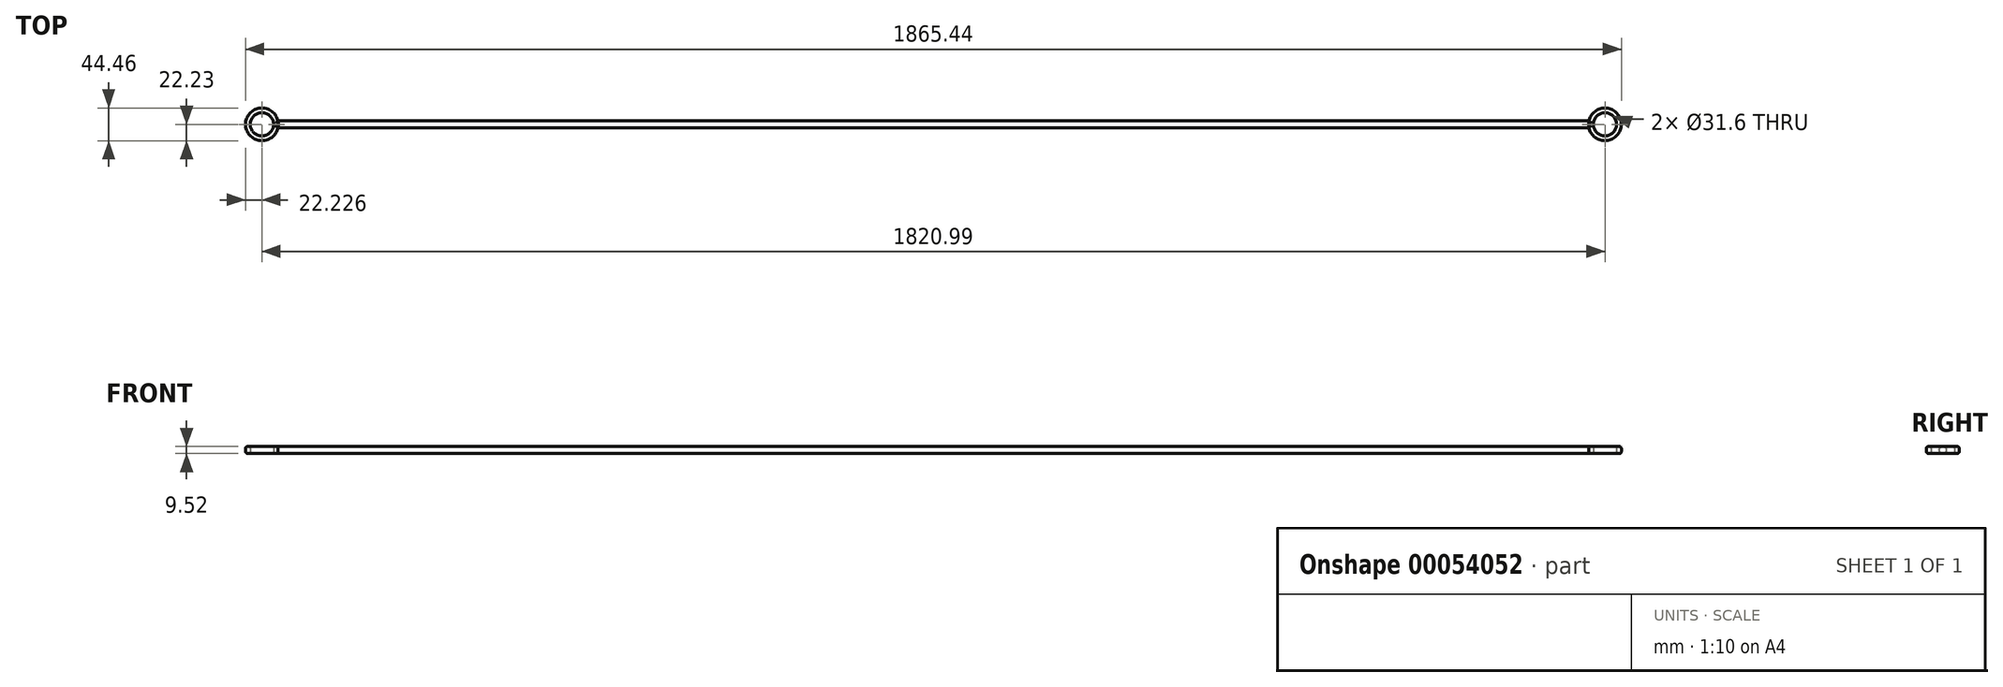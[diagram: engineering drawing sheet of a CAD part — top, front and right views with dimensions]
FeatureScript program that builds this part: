
annotation { "Feature Type Name" : "Feature", "Feature Type Description" : "" }
export const myFeature = defineFeature(function(context is Context, id is Id, definition is map)
    precondition{}
    {
        {
            var Q0;
            Q0=qCreatedBy(makeId("Right.planeOp"),FACE);
            var sketch = newSketch(context, id + "F0", { "sketchPlane" : qUnion([Q0])});
            skCircle(sketch, "E0", {"center": v(0, 0) * mm, "radius": 4.76 * mm});
            skSolve(sketch);
        }
        {
            var Q0;
            Q0=makeQuery(id+"F0.imprint","IMPRINT",FACE,{"disambiguationData":[TD([[makeQuery(id+"F0.imprint","IMPRINT",EDGE,{"derivedFrom":sQuery(id+"F0.wireOp",EDGE,"E0")}),1.0]])]});
            extrude(context, id + "F1", {"entities" : qUnion([Q0]), "depth" : 889 * mm});
        }
        {
            var Q0;
            Q0=qCreatedBy(makeId("Top.planeOp"),FACE);
            var sketch = newSketch(context, id + "F2", { "sketchPlane" : qUnion([Q0])});
            skCircle(sketch, "E1", {"center": v(-21.5, 0) * mm, "radius": 22.23 * mm});
            skCircle(sketch, "E2", {"center": v(-21.5, 0) * mm, "radius": 15.8 * mm});
            skSolve(sketch);
        }
        {
            var Q0;
            Q0=makeQuery(id+"F2.imprint","IMPRINT",FACE,{"disambiguationData":[TD([[makeQuery(id+"F2.imprint","IMPRINT",EDGE,{"derivedFrom":sQuery(id+"F2.wireOp",EDGE,"E1")}),1.0]])]});
            extrude(context, id + "F3", {"entities" : qUnion([Q0]), "operationType" : NewBodyOperationType.ADD, "depth" : 9.52 * mm, "symmetric" : true});
        }
        {
            var Q0;
            Q0=makeQuery(id+"F3.opExtrude","CAP_EDGE",EDGE,{"disambiguationData":[OSD([sQuery(id+"F2.wireOp",EDGE,"E2")])],"isStart":false});
            var Q1;
            Q1=makeQuery(id+"F3.opExtrude","CAP_EDGE",EDGE,{"disambiguationData":[OSD([sQuery(id+"F2.wireOp",EDGE,"E1")])],"isStart":false});
            var Q2;
            Q2=makeQuery(id+"F3.opExtrude","CAP_EDGE",EDGE,{"disambiguationData":[OSD([sQuery(id+"F2.wireOp",EDGE,"E2")])],"isStart":true});
            var Q3;
            Q3=makeQuery(id+"F3.opExtrude","CAP_FACE",FACE,{"disambiguationData":[OSD([sQuery(id+"F2.wireOp",EDGE,"E1"),sQuery(id+"F2.wireOp",EDGE,"E2")])],"isStart":true});
            fillet(context, id + "F4", {"entities" : qUnion([Q0, Q1, Q2, Q3]), "radius" : 2.54 * mm, "tangentPropagation" : true, "allowEdgeOverflow" : false});
        }
        {
            var Q0;
            Q0=qCreatedBy(makeId("Right.planeOp"),FACE);
            cPlane(context, id + "F5", {"entities" : qUnion([Q0]), "cplaneType" : CPlaneType.OFFSET, "offset" : 889 * mm, "width" : 152.4 * mm, "height" : 152.4 * mm});
        }
        {
            var Q0;
            Q0=makeQuery(id+"F1.opExtrude","SWEPT_BODY",BODY,{"disambiguationData":[OSD([sQuery(id+"F0.wireOp",EDGE,"E0")])]});
            var Q1;
            Q1=qCreatedBy(id+"F5.planeOp",FACE);
            mirror(context, id + "F6", {"operationType" : NewBodyOperationType.ADD, "entities" : qUnion([Q0]), "mirrorPlane" : qUnion([Q1])});
        }
    });
